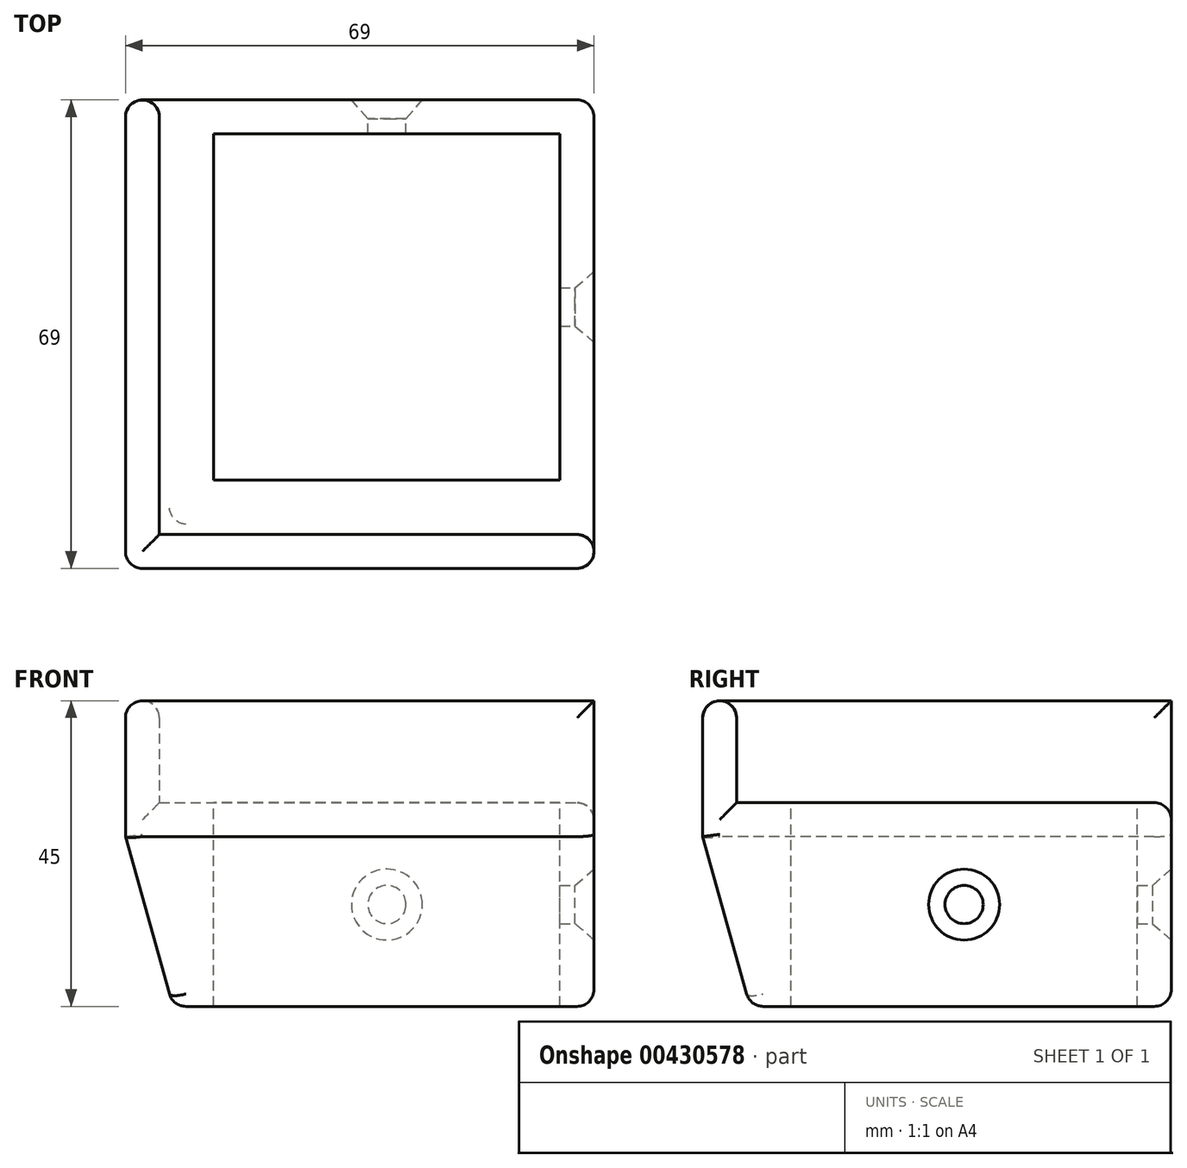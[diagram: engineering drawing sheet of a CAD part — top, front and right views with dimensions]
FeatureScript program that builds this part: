
annotation { "Feature Type Name" : "Feature", "Feature Type Description" : "" }
export const myFeature = defineFeature(function(context is Context, id is Id, definition is map)
    precondition{}
    {
        {
            var Q0;
            Q0=qCreatedBy(makeId("Top.planeOp"),FACE);
            var sketch = newSketch(context, id + "F0", { "sketchPlane" : qUnion([Q0])});
            skLineSegment(sketch, "E0.bottom", {"start": v(25.5, -25.5) * mm, "end": v(-25.5, -25.5) * mm});
            skLineSegment(sketch, "E0.top", {"start": v(25.5, 25.5) * mm, "end": v(-25.5, 25.5) * mm});
            skLineSegment(sketch, "E0.left", {"start": v(25.5, -25.5) * mm, "end": v(25.5, 25.5) * mm});
            skLineSegment(sketch, "E0.right", {"start": v(-25.5, -25.5) * mm, "end": v(-25.5, 25.5) * mm});
            skPoint(sketch, "E0.middle", {"position": v(0, 0) * mm});
            skLineSegment(sketch, "E1.bottom", {"start": v(-38.5, 30.5) * mm, "end": v(30.5, 30.5) * mm});
            skLineSegment(sketch, "E1.top", {"start": v(-38.5, -38.5) * mm, "end": v(30.5, -38.5) * mm});
            skLineSegment(sketch, "E1.left", {"start": v(-38.5, 30.5) * mm, "end": v(-38.5, -38.5) * mm});
            skLineSegment(sketch, "E1.right", {"start": v(30.5, 30.5) * mm, "end": v(30.5, -38.5) * mm});
            skLineSegment(sketch, "E2.bottom", {"start": v(-38.5, 30.5) * mm, "end": v(-33.5, 30.5) * mm});
            skLineSegment(sketch, "E2.top", {"start": v(-38.5, -38.5) * mm, "end": v(-33.5, -38.5) * mm});
            skLineSegment(sketch, "E2.right", {"start": v(-33.5, 30.5) * mm, "end": v(-33.5, -38.5) * mm});
            skLineSegment(sketch, "E3.bottom", {"start": v(30.5, -38.5) * mm, "end": v(-38.5, -38.5) * mm});
            skLineSegment(sketch, "E3.top", {"start": v(30.5, -33.5) * mm, "end": v(-38.5, -33.5) * mm});
            skLineSegment(sketch, "E3.left", {"start": v(30.5, -38.5) * mm, "end": v(30.5, -33.5) * mm});
            skLineSegment(sketch, "E3.right", {"start": v(-38.5, -38.5) * mm, "end": v(-38.5, -33.5) * mm});
            skSolve(sketch);
        }
        {
            var Q0;
            Q0=makeQuery(id+"F0.imprint","IMPRINT",FACE,{"disambiguationData":[TD([[makeQuery(id+"F0.imprint","IMPRINT",EDGE,{"derivedFrom":sQuery(id+"F0.wireOp",EDGE,"E0.bottom")}),1.0]])]});
            var Q1;
            {var subQ0=sQuery(id+"F0.wireOp",EDGE,"E2.right");var subQ1=sQuery(id+"F0.wireOp",EDGE,"E1.bottom");var subQ2=makeQuery(id+"F0.imprint","INTERSECT",VERTEX,{"derivedFrom":[subQ1,subQ0]});Q1=makeQuery(id+"F0.imprint","IMPRINT",FACE,{"disambiguationData":[TD([[makeQuery(id+"F0.imprint","IMPRINT",EDGE,{"disambiguationData":[TD([[subQ2,1.0]])],"derivedFrom":subQ1}),-1.0]])]});}
            var Q2;
            {var subQ0=sQuery(id+"F0.wireOp",EDGE,"E2.right");var subQ1=sQuery(id+"F0.wireOp",EDGE,"E1.top");var subQ2=makeQuery(id+"F0.imprint","INTERSECT",VERTEX,{"derivedFrom":[subQ1,subQ0]});Q2=makeQuery(id+"F0.imprint","IMPRINT",FACE,{"disambiguationData":[TD([[makeQuery(id+"F0.imprint","IMPRINT",EDGE,{"disambiguationData":[TD([[subQ2,1.0]])],"derivedFrom":subQ1}),1.0]])]});}
            var Q3;
            {var subQ0=sQuery(id+"F0.wireOp",EDGE,"E2.right");var subQ1=sQuery(id+"F0.wireOp",EDGE,"E1.top");var subQ2=makeQuery(id+"F0.imprint","INTERSECT",VERTEX,{"derivedFrom":[subQ1,subQ0]});Q3=makeQuery(id+"F0.imprint","IMPRINT",FACE,{"disambiguationData":[TD([[makeQuery(id+"F0.imprint","IMPRINT",EDGE,{"disambiguationData":[TD([[subQ2,-1.0]])],"derivedFrom":subQ1}),1.0]])]});}
            extrude(context, id + "F1", {"entities" : qUnion([Q0, Q1, Q2, Q3]), "oppositeDirection" : true, "depth" : 30 * mm, "offsetDistance" : 25 * mm});
        }
        {
            var Q0;
            {var subQ0=sQuery(id+"F0.wireOp",EDGE,"E2.right");var subQ1=sQuery(id+"F0.wireOp",EDGE,"E1.bottom");var subQ2=makeQuery(id+"F0.imprint","INTERSECT",VERTEX,{"derivedFrom":[subQ1,subQ0]});Q0=makeQuery(id+"F0.imprint","IMPRINT",FACE,{"disambiguationData":[TD([[makeQuery(id+"F0.imprint","IMPRINT",EDGE,{"disambiguationData":[TD([[subQ2,1.0]])],"derivedFrom":subQ1}),-1.0]])]});}
            var Q1;
            {var subQ0=sQuery(id+"F0.wireOp",EDGE,"E2.right");var subQ1=sQuery(id+"F0.wireOp",EDGE,"E1.top");var subQ2=makeQuery(id+"F0.imprint","INTERSECT",VERTEX,{"derivedFrom":[subQ1,subQ0]});Q1=makeQuery(id+"F0.imprint","IMPRINT",FACE,{"disambiguationData":[TD([[makeQuery(id+"F0.imprint","IMPRINT",EDGE,{"disambiguationData":[TD([[subQ2,1.0]])],"derivedFrom":subQ1}),1.0]])]});}
            var Q2;
            {var subQ0=sQuery(id+"F0.wireOp",EDGE,"E2.right");var subQ1=sQuery(id+"F0.wireOp",EDGE,"E1.top");var subQ2=makeQuery(id+"F0.imprint","INTERSECT",VERTEX,{"derivedFrom":[subQ1,subQ0]});Q2=makeQuery(id+"F0.imprint","IMPRINT",FACE,{"disambiguationData":[TD([[makeQuery(id+"F0.imprint","IMPRINT",EDGE,{"disambiguationData":[TD([[subQ2,-1.0]])],"derivedFrom":subQ1}),1.0]])]});}
            extrude(context, id + "F2", {"entities" : qUnion([Q0, Q1, Q2]), "operationType" : NewBodyOperationType.ADD, "depth" : 15 * mm, "offsetDistance" : 25 * mm});
        }
        {
            var Q0;
            Q0=makeQuery(id+"F1.opExtrude","CAP_EDGE",EDGE,{"disambiguationData":[OSD([sQuery(id+"F0.wireOp",EDGE,"E1.left")])],"isStart":false});
            var Q1;
            Q1=makeQuery(id+"F1.opExtrude","CAP_EDGE",EDGE,{"disambiguationData":[OSD([sQuery(id+"F0.wireOp",EDGE,"E1.top")])],"isStart":false});
            chamfer(context, id + "F3", {"entities" : qUnion([Q0, Q1]), "chamferType" : ChamferType.TWO_OFFSETS, "width1" : 25 * mm, "oppositeDirection" : false, "width2" : 7 * mm, "tangentPropagation" : true});
        }
        {
            var Q0;
            Q0=makeQuery(id+"F2.opExtrude","CAP_EDGE",EDGE,{"disambiguationData":[OSD([sQuery(id+"F0.wireOp",EDGE,"E1.top")])],"isStart":false});
            var Q1;
            Q1=makeQuery(id+"F2.opExtrude","CAP_EDGE",EDGE,{"disambiguationData":[OSD([sQuery(id+"F0.wireOp",EDGE,"E3.top")])],"isStart":false});
            var Q2;
            Q2=makeQuery(id+"F2.opExtrude","CAP_EDGE",EDGE,{"disambiguationData":[OSD([sQuery(id+"F0.wireOp",EDGE,"E1.left")])],"isStart":false});
            var Q3;
            Q3=makeQuery(id+"F2.opExtrude","CAP_EDGE",EDGE,{"disambiguationData":[OSD([sQuery(id+"F0.wireOp",EDGE,"E2.right")])],"isStart":false});
            var Q4;
            Q4=makeQuery(id+"F1.opExtrude","CAP_EDGE",EDGE,{"disambiguationData":[OSD([sQuery(id+"F0.wireOp",EDGE,"E1.right")])],"isStart":true});
            var Q5;
            Q5=makeQuery(id+"F1.opExtrude","CAP_EDGE",EDGE,{"disambiguationData":[OSD([sQuery(id+"F0.wireOp",EDGE,"E1.bottom")])],"isStart":true});
            var Q6;
            {var subQ0=sQuery(id+"F0.wireOp",EDGE,"E1.bottom");Q6=makeQuery(id+"F3.opChamfer","BLEND_EDGE",EDGE,{"blendedFrom":[makeQuery(id+"F1.opExtrude","CAP_EDGE",EDGE,{"disambiguationData":[OSD([sQuery(id+"F0.wireOp",EDGE,"E1.left")])],"isStart":false}),makeQuery(id+"F2.boolean.opBoolean","MERGE",FACE,{"derivedFrom":[makeQuery(id+"F1.opExtrude","SWEPT_FACE",FACE,{"disambiguationData":[OSD([subQ0])]}),makeQuery(id+"F2.opExtrude","SWEPT_FACE",FACE,{"disambiguationData":[OSD([subQ0])]})]})],"blendedInto":[makeQuery(id+"F2.boolean.opBoolean","MERGE",FACE,{"derivedFrom":[makeQuery(id+"F1.opExtrude","SWEPT_FACE",FACE,{"disambiguationData":[OSD([subQ0])]}),makeQuery(id+"F2.opExtrude","SWEPT_FACE",FACE,{"disambiguationData":[OSD([subQ0])]})]})]});}
            var Q7;
            Q7=makeQuery(id+"F3.opChamfer","BLEND_EDGE",EDGE,{"blendedFrom":[makeQuery(id+"F1.opExtrude","CAP_EDGE",EDGE,{"disambiguationData":[OSD([sQuery(id+"F0.wireOp",EDGE,"E1.top")])],"isStart":false}),makeQuery(id+"F1.opExtrude","CAP_EDGE",EDGE,{"disambiguationData":[OSD([sQuery(id+"F0.wireOp",EDGE,"E1.left")])],"isStart":false})],"blendedInto":[]});
            var Q8;
            {var subQ0=sQuery(id+"F0.wireOp",EDGE,"E1.right");Q8=makeQuery(id+"F3.opChamfer","BLEND_EDGE",EDGE,{"blendedFrom":[makeQuery(id+"F1.opExtrude","CAP_EDGE",EDGE,{"disambiguationData":[OSD([sQuery(id+"F0.wireOp",EDGE,"E1.top")])],"isStart":false}),makeQuery(id+"F2.boolean.opBoolean","MERGE",FACE,{"derivedFrom":[makeQuery(id+"F1.opExtrude","SWEPT_FACE",FACE,{"disambiguationData":[OSD([subQ0])]}),makeQuery(id+"F2.opExtrude","SWEPT_FACE",FACE,{"disambiguationData":[OSD([subQ0])]})]})],"blendedInto":[makeQuery(id+"F2.boolean.opBoolean","MERGE",FACE,{"derivedFrom":[makeQuery(id+"F1.opExtrude","SWEPT_FACE",FACE,{"disambiguationData":[OSD([subQ0])]}),makeQuery(id+"F2.opExtrude","SWEPT_FACE",FACE,{"disambiguationData":[OSD([subQ0])]})]})]});}
            var Q9;
            Q9=makeQuery(id+"F1.opExtrude","SWEPT_EDGE",EDGE,{"disambiguationData":[OSD([sQuery(id+"F0.wireOp",EDGE,"E1.bottom"),sQuery(id+"F0.wireOp",EDGE,"E1.right")])]});
            var Q10;
            Q10=makeQuery(id+"F2.opExtrude","SWEPT_EDGE",EDGE,{"disambiguationData":[OSD([sQuery(id+"F0.wireOp",EDGE,"E1.bottom"),sQuery(id+"F0.wireOp",EDGE,"E2.right")])]});
            var Q11;
            {var subQ0=sQuery(id+"F0.wireOp",EDGE,"E1.left");var subQ1=sQuery(id+"F0.wireOp",EDGE,"E1.top");Q11=makeQuery(id+"F2.boolean.opBoolean","MERGE",EDGE,{"derivedFrom":[makeQuery(id+"F1.opExtrude","SWEPT_EDGE",EDGE,{"disambiguationData":[OSD([subQ1,subQ0])]}),makeQuery(id+"F2.opExtrude","SWEPT_EDGE",EDGE,{"disambiguationData":[OSD([subQ1,subQ0])]})]});}
            var Q12;
            {var subQ0=sQuery(id+"F0.wireOp",EDGE,"E1.right");var subQ1=sQuery(id+"F0.wireOp",EDGE,"E1.top");Q12=makeQuery(id+"F2.boolean.opBoolean","MERGE",EDGE,{"derivedFrom":[makeQuery(id+"F1.opExtrude","SWEPT_EDGE",EDGE,{"disambiguationData":[OSD([subQ1,subQ0])]}),makeQuery(id+"F2.opExtrude","SWEPT_EDGE",EDGE,{"disambiguationData":[OSD([subQ1,subQ0])]})]});}
            var Q13;
            {var subQ0=sQuery(id+"F0.wireOp",EDGE,"E1.left");var subQ1=sQuery(id+"F0.wireOp",EDGE,"E1.bottom");Q13=makeQuery(id+"F2.boolean.opBoolean","MERGE",EDGE,{"derivedFrom":[makeQuery(id+"F1.opExtrude","SWEPT_EDGE",EDGE,{"disambiguationData":[OSD([subQ1,subQ0])]}),makeQuery(id+"F2.opExtrude","SWEPT_EDGE",EDGE,{"disambiguationData":[OSD([subQ1,subQ0])]})]});}
            var Q14;
            Q14=makeQuery(id+"F2.opExtrude","SWEPT_EDGE",EDGE,{"disambiguationData":[OSD([sQuery(id+"F0.wireOp",EDGE,"E1.right"),sQuery(id+"F0.wireOp",EDGE,"E3.top")])]});
            var Q15;
            Q15=makeQuery(id+"F1.opExtrude","CAP_EDGE",EDGE,{"disambiguationData":[OSD([sQuery(id+"F0.wireOp",EDGE,"E1.right")])],"isStart":false});
            var Q16;
            {var subQ0=sQuery(id+"F0.wireOp",EDGE,"E1.top");Q16=makeQuery(id+"F3.opChamfer","BLEND_EDGE",EDGE,{"blendedFrom":[makeQuery(id+"F1.opExtrude","CAP_EDGE",EDGE,{"disambiguationData":[OSD([subQ0])],"isStart":false}),makeQuery(id+"F1.opExtrude","CAP_FACE",FACE,{"disambiguationData":[OSD([sQuery(id+"F0.wireOp",EDGE,"E0.bottom"),sQuery(id+"F0.wireOp",EDGE,"E0.top"),sQuery(id+"F0.wireOp",EDGE,"E0.left"),sQuery(id+"F0.wireOp",EDGE,"E0.right"),sQuery(id+"F0.wireOp",EDGE,"E1.bottom"),subQ0,sQuery(id+"F0.wireOp",EDGE,"E1.left"),sQuery(id+"F0.wireOp",EDGE,"E1.right")])],"isStart":false})],"blendedInto":[makeQuery(id+"F1.opExtrude","CAP_FACE",FACE,{"disambiguationData":[OSD([sQuery(id+"F0.wireOp",EDGE,"E0.bottom"),sQuery(id+"F0.wireOp",EDGE,"E0.top"),sQuery(id+"F0.wireOp",EDGE,"E0.left"),sQuery(id+"F0.wireOp",EDGE,"E0.right"),sQuery(id+"F0.wireOp",EDGE,"E1.bottom"),subQ0,sQuery(id+"F0.wireOp",EDGE,"E1.left"),sQuery(id+"F0.wireOp",EDGE,"E1.right")])],"isStart":false})]});}
            var Q17;
            Q17=makeQuery(id+"F1.opExtrude","CAP_EDGE",EDGE,{"disambiguationData":[OSD([sQuery(id+"F0.wireOp",EDGE,"E1.bottom")])],"isStart":false});
            var Q18;
            {var subQ0=sQuery(id+"F0.wireOp",EDGE,"E1.left");Q18=makeQuery(id+"F3.opChamfer","BLEND_EDGE",EDGE,{"blendedFrom":[makeQuery(id+"F1.opExtrude","CAP_EDGE",EDGE,{"disambiguationData":[OSD([subQ0])],"isStart":false}),makeQuery(id+"F1.opExtrude","CAP_FACE",FACE,{"disambiguationData":[OSD([sQuery(id+"F0.wireOp",EDGE,"E0.bottom"),sQuery(id+"F0.wireOp",EDGE,"E0.top"),sQuery(id+"F0.wireOp",EDGE,"E0.left"),sQuery(id+"F0.wireOp",EDGE,"E0.right"),sQuery(id+"F0.wireOp",EDGE,"E1.bottom"),sQuery(id+"F0.wireOp",EDGE,"E1.top"),subQ0,sQuery(id+"F0.wireOp",EDGE,"E1.right")])],"isStart":false})],"blendedInto":[makeQuery(id+"F1.opExtrude","CAP_FACE",FACE,{"disambiguationData":[OSD([sQuery(id+"F0.wireOp",EDGE,"E0.bottom"),sQuery(id+"F0.wireOp",EDGE,"E0.top"),sQuery(id+"F0.wireOp",EDGE,"E0.left"),sQuery(id+"F0.wireOp",EDGE,"E0.right"),sQuery(id+"F0.wireOp",EDGE,"E1.bottom"),sQuery(id+"F0.wireOp",EDGE,"E1.top"),subQ0,sQuery(id+"F0.wireOp",EDGE,"E1.right")])],"isStart":false})]});}
            fillet(context, id + "F4", {"entities" : qUnion([Q0, Q1, Q2, Q3, Q4, Q5, Q6, Q7, Q8, Q9, Q10, Q11, Q12, Q13, Q14, Q15, Q16, Q17, Q18]), "tangentPropagation" : true, "radius" : 2.5 * mm, "defaultsChanged" : false, "vertexSettings" : [], "allowEdgeOverflow" : false});
        }
        {
            var Q0;
            {var subQ0=sQuery(id+"F0.wireOp",EDGE,"E1.right");Q0=makeQuery(id+"F2.boolean.opBoolean","MERGE",FACE,{"derivedFrom":[makeQuery(id+"F1.opExtrude","SWEPT_FACE",FACE,{"disambiguationData":[OSD([subQ0])]}),makeQuery(id+"F2.opExtrude","SWEPT_FACE",FACE,{"disambiguationData":[OSD([subQ0])]})]});}
            var sketch = newSketch(context, id + "F5", { "sketchPlane" : qUnion([Q0])});
            skPoint(sketch, "E4", {"position": v(0, -15) * mm});
            skSolve(sketch);
        }
        {
            var Q0;
            {var subQ0=sQuery(id+"F0.wireOp",EDGE,"E1.bottom");Q0=makeQuery(id+"F2.boolean.opBoolean","MERGE",FACE,{"derivedFrom":[makeQuery(id+"F1.opExtrude","SWEPT_FACE",FACE,{"disambiguationData":[OSD([subQ0])]}),makeQuery(id+"F2.opExtrude","SWEPT_FACE",FACE,{"disambiguationData":[OSD([subQ0])]})]});}
            var sketch = newSketch(context, id + "F6", { "sketchPlane" : qUnion([Q0])});
            skPoint(sketch, "E5", {"position": v(0, -15) * mm});
            skSolve(sketch);
        }
        {
            var Q0;
            Q0=sQuery(id+"F5.wireOp",VERTEX,"E4");
            var Q1;
            Q1=sQuery(id+"F6.wireOp",VERTEX,"E5");
            var Q2;
            Q2=makeQuery(id+"F1.opExtrude","SWEPT_BODY",BODY,{"disambiguationData":[OSD([sQuery(id+"F0.wireOp",EDGE,"E0.bottom"),sQuery(id+"F0.wireOp",EDGE,"E0.top"),sQuery(id+"F0.wireOp",EDGE,"E0.left"),sQuery(id+"F0.wireOp",EDGE,"E0.right"),sQuery(id+"F0.wireOp",EDGE,"E1.bottom"),sQuery(id+"F0.wireOp",EDGE,"E1.top"),sQuery(id+"F0.wireOp",EDGE,"E1.left"),sQuery(id+"F0.wireOp",EDGE,"E1.right")])]});
            hole(context, id + "F7", {"style" : HoleStyle.C_SINK, "endStyle" : HoleEndStyle.BLIND, "standardTappedOrClearance" : lookupTablePath({ "fit" : "Normal (ASME)", "standard" : "ANSI", "size" : "#10", "type" : "Clearance" }), "standardBlindInLast" : lookupTablePath({ "fit" : "Normal (ASME)", "standard" : "ANSI", "engagement" : "75%", "pitch" : "24 tpi", "size" : "#10", "type" : "Clearance & tapped" }), "holeDiameter" : 5.61 * mm, "cSinkDiameter" : 10.44 * mm, "cSinkAngle" : 82 * degree, "majorDiameter" : 5 * mm, "holeDepth" : 12 * mm, "isTappedThrough" : true, "tappedDepth" : 12 * mm, "tapClearance" : 3, "locations" : qUnion([Q0, Q1]), "scope" : qUnion([Q2])});
        }
    });
